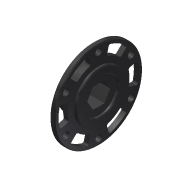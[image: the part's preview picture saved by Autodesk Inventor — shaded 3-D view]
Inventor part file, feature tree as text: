
AUTODESK INVENTOR PART (.ipt)
format: ipt  version: 2015 (Build 190159000, 159)  size: 236,032 bytes
history: native  units: in
note: dims shown in document units (in); Inventor stores cm internally (conversion verified against a paired STEP export)
features: imported_body x2, sketch x2, extrude x1, hole x1, pattern_circular x1
ambient origin geometry x8: Origin, YZ Plane, XZ Plane, XY Plane, X Axis, Y Axis, Z Axis, Center Point
bodies: Body1 (feature_tree)
feature tree (7):
  imported_body  "Imported1"
  extrude  "Extrusion1"  Depth=0.9375in
  hole  "Hole1"  [1 undecoded]
  pattern_circular  "Circular Pattern1"  [2 undecoded]
  imported_body  "Base1"
  sketch  "Sketch1"  dims[d0=1.0in d1=0.0in d2=0.9375in]
  sketch  "Sketch2"  dims[d3=0.169in d4=0.75in d5=0.375in d6=0.25in d7=0.5635in d8=1.0in d9=0.8108in d10=2.3622in d11=360.0deg]
note: 3 required parameter values undecoded (feature->parameter linkage not recoverable at this tier; creation-order binding heuristic only, values carry confidence <= 0.55)
